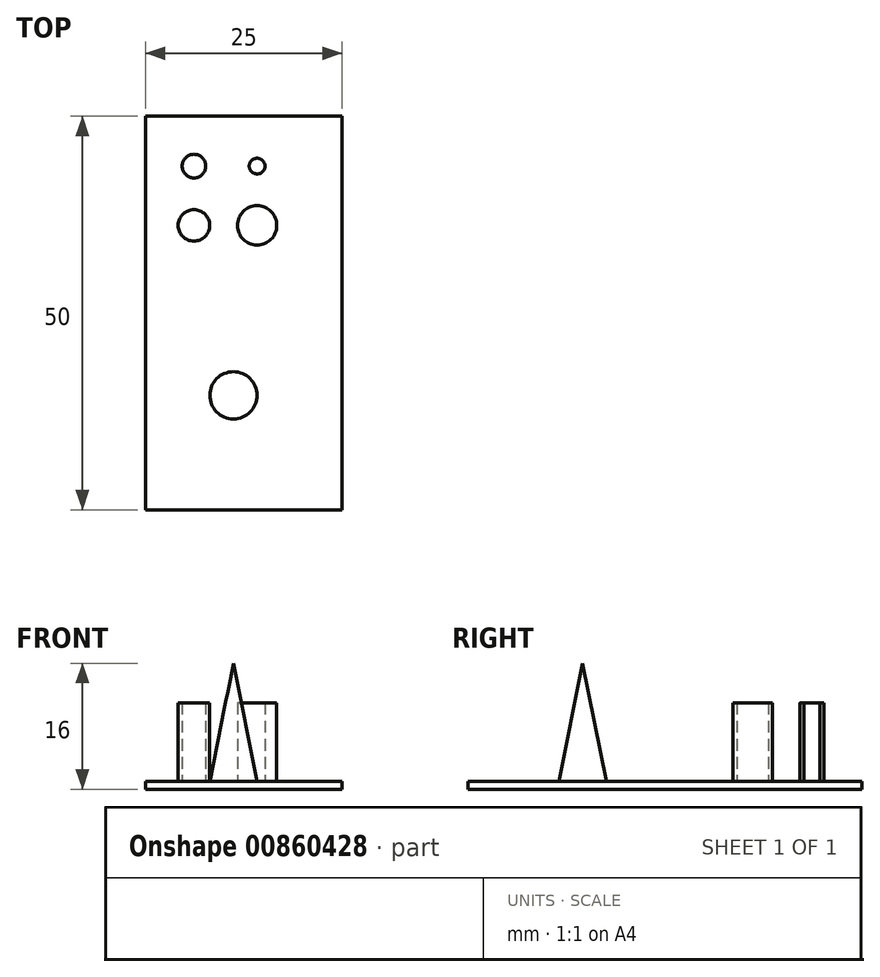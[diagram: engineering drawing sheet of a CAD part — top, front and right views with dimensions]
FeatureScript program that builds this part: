
annotation { "Feature Type Name" : "Feature", "Feature Type Description" : "" }
export const myFeature = defineFeature(function(context is Context, id is Id, definition is map)
    precondition{}
    {
        {
            var Q0;
            Q0=qCreatedBy(makeId("Top.planeOp"),FACE);
            var sketch = newSketch(context, id + "F0", { "sketchPlane" : qUnion([Q0])});
            skLineSegment(sketch, "E0.bottom", {"start": v(25, -25) * mm, "end": v(-25, -25) * mm});
            skLineSegment(sketch, "E0.top", {"start": v(25, 25) * mm, "end": v(-25, 25) * mm});
            skLineSegment(sketch, "E0.left", {"start": v(25, -25) * mm, "end": v(25, 25) * mm});
            skLineSegment(sketch, "E0.right", {"start": v(-25, -25) * mm, "end": v(-25, 25) * mm});
            skPoint(sketch, "E0.middle", {"position": v(0, 0) * mm});
            skSolve(sketch);
        }
        {
            var Q0;
            Q0 = qSketchRegion(id + "F0", true);
            extrude(context, id + "F1", {"entities" : qUnion([Q0]), "depth" : 1 * mm, "offsetDistance" : 25 * mm});
        }
        {
            var Q0;
            Q0=makeQuery(id+"F1.opExtrude","CAP_FACE",FACE,{"disambiguationData":[OSD([sQuery(id+"F0.wireOp",EDGE,"E0.bottom"),sQuery(id+"F0.wireOp",EDGE,"E0.top"),sQuery(id+"F0.wireOp",EDGE,"E0.left"),sQuery(id+"F0.wireOp",EDGE,"E0.right")])],"isStart":false});
            var sketch = newSketch(context, id + "F2", { "sketchPlane" : qUnion([Q0])});
            skCircle(sketch, "E1", {"center": v(-18.83, 18.67) * mm, "radius": 1.5 * mm});
            skCircle(sketch, "E2", {"center": v(-10.8, 18.67) * mm, "radius": 1 * mm});
            skCircle(sketch, "E3", {"center": v(-18.83, 11.13) * mm, "radius": 2 * mm});
            skCircle(sketch, "E4", {"center": v(-10.8, 11.13) * mm, "radius": 2.5 * mm});
            skSolve(sketch);
        }
        {
            var Q0;
            Q0 = qSketchRegion(id + "F2", true);
            extrude(context, id + "F3", {"entities" : qUnion([Q0]), "operationType" : NewBodyOperationType.ADD, "depth" : 10 * mm, "offsetDistance" : 25 * mm});
        }
        {
            var Q0;
            Q0=makeQuery(id+"F1.opExtrude","CAP_FACE",FACE,{"disambiguationData":[OSD([sQuery(id+"F0.wireOp",EDGE,"E0.bottom"),sQuery(id+"F0.wireOp",EDGE,"E0.top"),sQuery(id+"F0.wireOp",EDGE,"E0.left"),sQuery(id+"F0.wireOp",EDGE,"E0.right")])],"isStart":false});
            var sketch = newSketch(context, id + "F4", { "sketchPlane" : qUnion([Q0])});
            skCircle(sketch, "E5", {"center": v(-13.8, -10.45) * mm, "radius": 3 * mm});
            skSolve(sketch);
        }
        {
            var Q0;
            Q0=makeQuery(id+"F4.imprint","IMPRINT",FACE,{"disambiguationData":[TD([[makeQuery(id+"F4.imprint","IMPRINT",EDGE,{"derivedFrom":sQuery(id+"F4.wireOp",EDGE,"E5")}),-1.0]])]});
            cPlane(context, id + "F5", {"entities" : qUnion([Q0]), "cplaneType" : CPlaneType.OFFSET, "offset" : 15 * mm, "width" : 150 * mm, "height" : 150 * mm});
        }
        {
            var Q0;
            Q0=qCreatedBy(id+"F5.planeOp",FACE);
            var sketch = newSketch(context, id + "F6", { "sketchPlane" : qUnion([Q0])});
            skPoint(sketch, "E6.0", {"position": v(-13.8, -10.45) * mm});
            skSolve(sketch);
        }
        {
            var Q1;
            Q1=makeQuery(id+"F4.imprint","IMPRINT",FACE,{"disambiguationData":[TD([[makeQuery(id+"F4.imprint","IMPRINT",EDGE,{"derivedFrom":sQuery(id+"F4.wireOp",EDGE,"E5")}),1.0]])]});
            var Q2;
            Q2=sQuery(id+"F6.wireOp",VERTEX,"E6.0");
            loft(context, id + "F7", {"operationType" : NewBodyOperationType.ADD, "sheetProfilesArray" : [{ "sheetProfileEntities" : qUnion([Q1]) }, { "sheetProfileEntities" : qUnion([Q2]) }]});
        }
        {
            var Q0;
            Q0=makeQuery(id+"F1.opExtrude","CAP_FACE",FACE,{"disambiguationData":[OSD([sQuery(id+"F0.wireOp",EDGE,"E0.bottom"),sQuery(id+"F0.wireOp",EDGE,"E0.top"),sQuery(id+"F0.wireOp",EDGE,"E0.left"),sQuery(id+"F0.wireOp",EDGE,"E0.right")])],"isStart":false});
            var sketch = newSketch(context, id + "F8", { "sketchPlane" : qUnion([Q0])});
            skLineSegment(sketch, "E7.bottom", {"start": v(25, 25) * mm, "end": v(0, 25) * mm});
            skLineSegment(sketch, "E7.top", {"start": v(25, -25) * mm, "end": v(0, -25) * mm});
            skLineSegment(sketch, "E7.left", {"start": v(25, 25) * mm, "end": v(25, -25) * mm});
            skLineSegment(sketch, "E7.right", {"start": v(0, 25) * mm, "end": v(0, -25) * mm});
            skSolve(sketch);
        }
        {
            var Q0;
            Q0 = qSketchRegion(id + "F8", true);
            var Q1;
            Q1=makeQuery(id+"F1.opExtrude","CAP_FACE",FACE,{"disambiguationData":[OSD([sQuery(id+"F0.wireOp",EDGE,"E0.bottom"),sQuery(id+"F0.wireOp",EDGE,"E0.top"),sQuery(id+"F0.wireOp",EDGE,"E0.left"),sQuery(id+"F0.wireOp",EDGE,"E0.right")])],"isStart":true});
            extrude(context, id + "F9", {"entities" : qUnion([Q0]), "operationType" : NewBodyOperationType.REMOVE, "endBound" : BoundingType.UP_TO_SURFACE, "oppositeDirection" : true, "depth" : 25 * mm, "endBoundEntityFace" : qUnion([Q1]), "offsetDistance" : 25 * mm});
        }
    });
